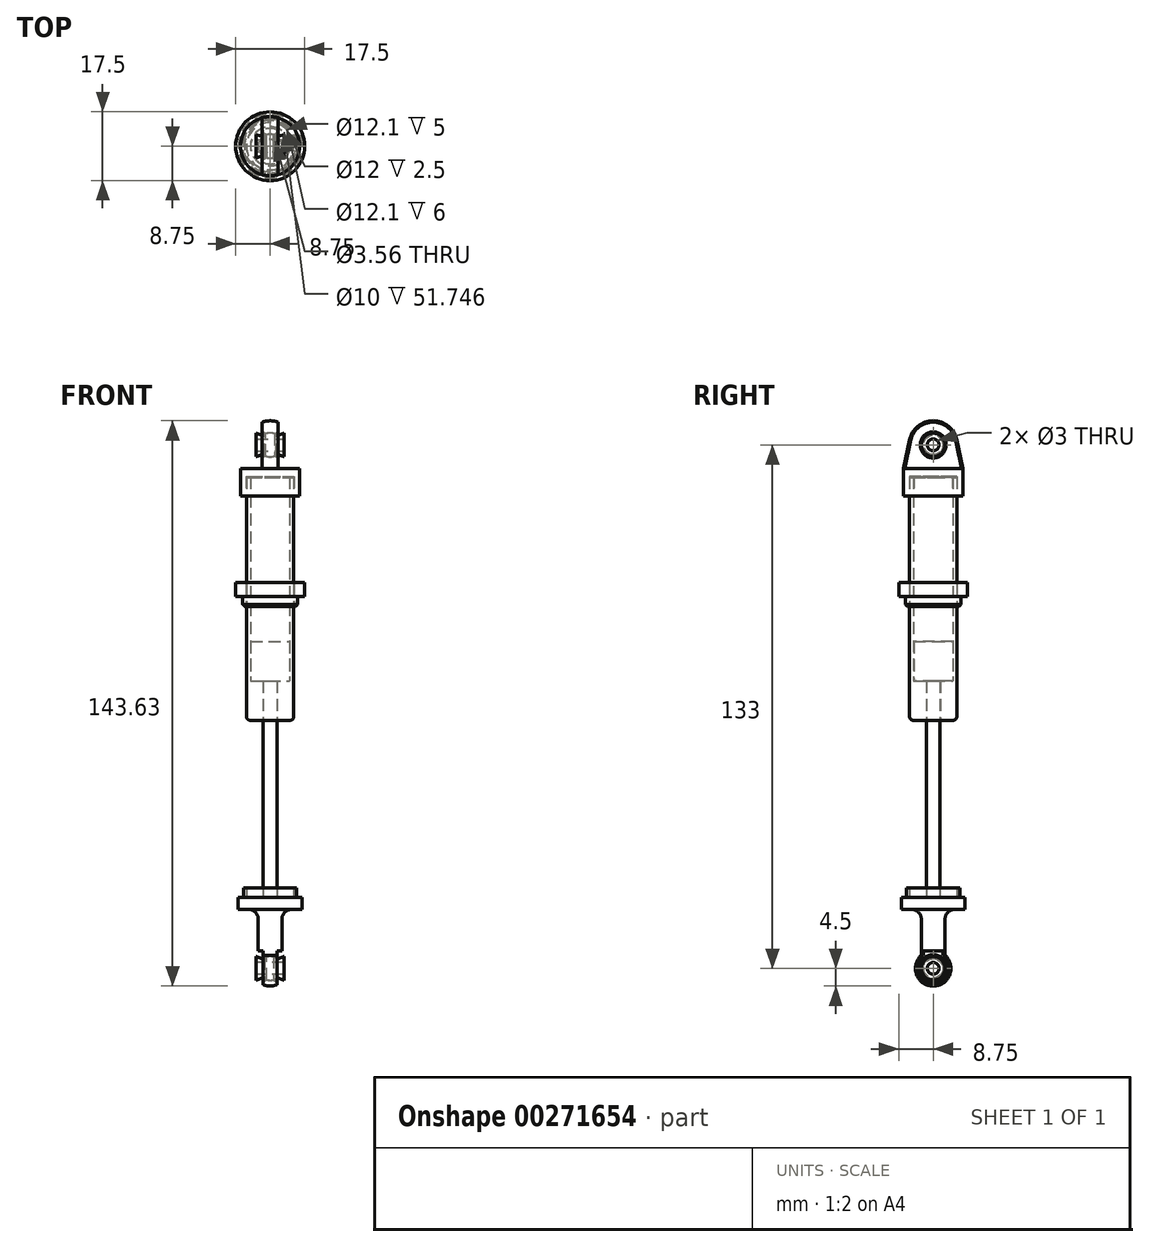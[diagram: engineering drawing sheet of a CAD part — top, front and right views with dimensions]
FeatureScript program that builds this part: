
annotation { "Feature Type Name" : "Feature", "Feature Type Description" : "" }
export const myFeature = defineFeature(function(context is Context, id is Id, definition is map)
    precondition{}
    {
        {
            var Q0;
            Q0=qCreatedBy(makeId("Front.planeOp"),FACE);
            var sketch = newSketch(context, id + "F0", { "sketchPlane" : qUnion([Q0])});
            skLineSegment(sketch, "E0", {"start": v(0, 0) * mm, "end": v(0, 317.47) * mm, "construction": true});
            skArc(sketch, "E1", {"start": v(0, 3) * mm, "mid": v(-3, 0) * mm, "end": v(0, -3) * mm});
            skLineSegment(sketch, "E2", {"start": v(0, 3) * mm, "end": v(0, -3) * mm});
            skArc(sketch, "E3", {"start": v(0, 3.05) * mm, "mid": v(-3.05, 0) * mm, "end": v(0, -3.05) * mm});
            skLineSegment(sketch, "E4", {"start": v(0, -3.05) * mm, "end": v(0, -4.5) * mm});
            skArc(sketch, "E5", {"start": v(-3, 3.35) * mm, "mid": v(-4.2, -1.6) * mm, "end": v(0, -4.5) * mm});
            skLineSegment(sketch, "E6", {"start": v(-3, 3.35) * mm, "end": v(-3, 12.46) * mm});
            skArc(sketch, "E7", {"start": v(-3, 12.46) * mm, "mid": v(-3.74, 14.26) * mm, "end": v(-5.54, 15) * mm});
            skLineSegment(sketch, "E8", {"start": v(-5.54, 15) * mm, "end": v(-8.1, 15) * mm});
            skLineSegment(sketch, "E9", {"start": v(-8.1, 15) * mm, "end": v(-8.1, 18) * mm});
            skLineSegment(sketch, "E10", {"start": v(-8.1, 18) * mm, "end": v(-6.75, 18) * mm});
            skLineSegment(sketch, "E11", {"start": v(-6.75, 18) * mm, "end": v(-6.75, 20.5) * mm});
            skLineSegment(sketch, "E12", {"start": v(-6.75, 20.5) * mm, "end": v(-6, 20.5) * mm});
            skLineSegment(sketch, "E13", {"start": v(-6, 20.5) * mm, "end": v(-6, 18) * mm});
            skLineSegment(sketch, "E14", {"start": v(-6, 18) * mm, "end": v(-1.75, 18) * mm});
            skLineSegment(sketch, "E15", {"start": v(-1.75, 18) * mm, "end": v(-1.75, 73.03) * mm});
            skLineSegment(sketch, "E16", {"start": v(-1.75, 73.03) * mm, "end": v(-4.95, 73.03) * mm});
            skLineSegment(sketch, "E17", {"start": v(-4.95, 73.03) * mm, "end": v(-4.95, 83.03) * mm});
            skLineSegment(sketch, "E18", {"start": v(-4.95, 83.03) * mm, "end": v(0, 83.03) * mm});
            skLineSegment(sketch, "E19", {"start": v(0, 83.03) * mm, "end": v(0, 3.05) * mm});
            skLineSegment(sketch, "E20", {"start": v(-1.78, 63) * mm, "end": v(-5, 63) * mm});
            skLineSegment(sketch, "E21", {"start": v(-6, 64) * mm, "end": v(-6, 124.75) * mm});
            skLineSegment(sketch, "E22", {"start": v(-1.78, 63) * mm, "end": v(-1.78, 73) * mm});
            skLineSegment(sketch, "E23", {"start": v(-1.78, 73) * mm, "end": v(-5, 73) * mm});
            skLineSegment(sketch, "E24", {"start": v(-5, 73) * mm, "end": v(-5, 124.75) * mm});
            skLineSegment(sketch, "E25", {"start": v(-7.5, 120) * mm, "end": v(-7.5, 127) * mm});
            skLineSegment(sketch, "E26", {"start": v(-7.5, 127) * mm, "end": v(-6, 134.24) * mm});
            skArc(sketch, "E27", {"start": v(0, 139.13) * mm, "mid": v(-3.87, 137.75) * mm, "end": v(-6, 134.24) * mm});
            skArc(sketch, "E28", {"start": v(0, 136) * mm, "mid": v(-3, 133) * mm, "end": v(0, 130) * mm});
            skArc(sketch, "E29", {"start": v(0, 136.05) * mm, "mid": v(-3.05, 133) * mm, "end": v(0, 129.95) * mm});
            skLineSegment(sketch, "E30", {"start": v(0, 136) * mm, "end": v(0, 130) * mm});
            skLineSegment(sketch, "E31", {"start": v(0, 136.05) * mm, "end": v(0, 139.13) * mm});
            skLineSegment(sketch, "E32", {"start": v(0, 129.95) * mm, "end": v(0, 119.92) * mm});
            skPoint(sketch, "E33.visualSharp", {"position": v(-6, 63) * mm});
            skArc(sketch, "E33.filletArc", {"start": v(-6, 64) * mm, "mid": v(-5.7, 63.3) * mm, "end": v(-5, 63) * mm});
            skLineSegment(sketch, "E34", {"start": v(-6.05, 92) * mm, "end": v(-6.05, 98) * mm});
            skLineSegment(sketch, "E35", {"start": v(-6.05, 98) * mm, "end": v(-8.75, 98) * mm});
            skLineSegment(sketch, "E36", {"start": v(-8.75, 98) * mm, "end": v(-8.75, 94.5) * mm});
            skLineSegment(sketch, "E37", {"start": v(-8.75, 94.5) * mm, "end": v(-7, 94.5) * mm});
            skLineSegment(sketch, "E38", {"start": v(-7, 94.5) * mm, "end": v(-7, 92.5) * mm});
            skLineSegment(sketch, "E39", {"start": v(-7, 92.5) * mm, "end": v(-6.5, 92) * mm});
            skLineSegment(sketch, "E40", {"start": v(-6.5, 92) * mm, "end": v(-6.05, 92) * mm});
            skLineSegment(sketch, "E41", {"start": v(-6, 124.75) * mm, "end": v(-5, 124.75) * mm});
            skLineSegment(sketch, "E42", {"start": v(-7.5, 120) * mm, "end": v(-6.05, 120) * mm});
            skLineSegment(sketch, "E43", {"start": v(-6.05, 120) * mm, "end": v(-6.05, 125) * mm});
            skLineSegment(sketch, "E44", {"start": v(-6.05, 125) * mm, "end": v(-4.95, 125) * mm});
            skLineSegment(sketch, "E45", {"start": v(-4.95, 125) * mm, "end": v(-4.95, 119.92) * mm});
            skLineSegment(sketch, "E46", {"start": v(-4.95, 119.92) * mm, "end": v(0, 119.92) * mm});
            skSolve(sketch);
        }
        {
            var Q0;
            Q0=qSketchRegion(id+"F0",true);
            var Q1;
            Q1=sQuery(id+"F0.wireOp",EDGE,"E0");
            revolve(context, id + "F1", {"entities" : qUnion([Q0]), "axis" : qUnion([Q1]), "revolveType" : RevolveType.FULL});
        }
        {
            var Q0;
            Q0=qCreatedBy(makeId("Front.planeOp"),FACE);
            var sketch = newSketch(context, id + "F2", { "sketchPlane" : qUnion([Q0])});
            skLineSegment(sketch, "E47", {"start": v(0, -24.47) * mm, "end": v(0, 246.9) * mm, "construction": true});
            skLineSegment(sketch, "E48.bottom", {"start": v(-1.75, 4.5) * mm, "end": v(-17.5, 4.5) * mm});
            skLineSegment(sketch, "E48.top", {"start": v(-1.75, -4.5) * mm, "end": v(-17.5, -4.5) * mm});
            skLineSegment(sketch, "E48.left", {"start": v(-1.75, 4.5) * mm, "end": v(-1.75, -4.5) * mm});
            skLineSegment(sketch, "E48.right", {"start": v(-17.5, 4.5) * mm, "end": v(-17.5, -4.5) * mm});
            skLineSegment(sketch, "E49.MirrorCS", {"start": v(1.75, 4.5) * mm, "end": v(17.5, 4.5) * mm});
            skLineSegment(sketch, "E50.MirrorCS", {"start": v(1.75, 4.5) * mm, "end": v(1.75, -4.5) * mm});
            skLineSegment(sketch, "E51.MirrorCS", {"start": v(1.75, -4.5) * mm, "end": v(17.5, -4.5) * mm});
            skLineSegment(sketch, "E52.MirrorCS", {"start": v(17.5, 4.5) * mm, "end": v(17.5, -4.5) * mm});
            skLineSegment(sketch, "E53.bottom", {"start": v(-2, 139.13) * mm, "end": v(-17.5, 139.13) * mm});
            skLineSegment(sketch, "E53.top", {"start": v(-2, 127) * mm, "end": v(-17.5, 127) * mm});
            skLineSegment(sketch, "E53.left", {"start": v(-2, 139.13) * mm, "end": v(-2, 127) * mm});
            skLineSegment(sketch, "E53.right", {"start": v(-17.5, 139.13) * mm, "end": v(-17.5, 127) * mm});
            skLineSegment(sketch, "E54.MirrorCS", {"start": v(17.5, 139.13) * mm, "end": v(17.5, 127) * mm});
            skLineSegment(sketch, "E55.MirrorCS", {"start": v(2, 127) * mm, "end": v(17.5, 127) * mm});
            skLineSegment(sketch, "E56.MirrorCS", {"start": v(2, 139.13) * mm, "end": v(17.5, 139.13) * mm});
            skLineSegment(sketch, "E57.MirrorCS", {"start": v(2, 139.13) * mm, "end": v(2, 127) * mm});
            skSolve(sketch);
        }
        {
            var Q0;
            Q0=qSketchRegion(id+"F2",true);
            extrude(context, id + "F3", {"entities" : qUnion([Q0]), "operationType" : NewBodyOperationType.REMOVE, "endBound" : BoundingType.THROUGH_ALL, "oppositeDirection" : true, "depth" : 25.4 * mm, "hasSecondDirection" : true, "secondDirectionBound" : BoundingType.THROUGH_ALL, "secondDirectionOppositeDirection" : false, "secondDirectionDepth" : 25.4 * mm});
        }
        {
            var Q0;
            Q0=makeQuery(id+"F3.boolean.opBoolean","INTERSECT",EDGE,{"derivedFrom":[makeQuery(id+"F1.opRevolve","SWEPT_FACE",FACE,{"disambiguationData":[OSD([sQuery(id+"F0.wireOp",EDGE,"E3")])]}),makeQuery(id+"F3.opExtrude","SWEPT_FACE",FACE,{"disambiguationData":[OSD([sQuery(id+"F2.wireOp",EDGE,"E48.left")])]})]});
            var Q1;
            Q1=makeQuery(id+"F3.boolean.opBoolean","INTERSECT",EDGE,{"derivedFrom":[makeQuery(id+"F1.opRevolve","SWEPT_FACE",FACE,{"disambiguationData":[OSD([sQuery(id+"F0.wireOp",EDGE,"E3")])]}),makeQuery(id+"F3.opExtrude","SWEPT_FACE",FACE,{"disambiguationData":[OSD([sQuery(id+"F2.wireOp",EDGE,"E50.MirrorCS")])]})]});
            chamfer(context, id + "F4", {"entities" : qUnion([Q0, Q1]), "width" : 1 * mm, "tangentPropagation" : true});
        }
        {
            var Q0;
            Q0=makeQuery(id+"F3.boolean.opBoolean","INTERSECT",EDGE,{"derivedFrom":[makeQuery(id+"F1.opRevolve","SWEPT_FACE",FACE,{"disambiguationData":[OSD([sQuery(id+"F0.wireOp",EDGE,"E29")])]}),makeQuery(id+"F3.opExtrude","SWEPT_FACE",FACE,{"disambiguationData":[OSD([sQuery(id+"F2.wireOp",EDGE,"E57.MirrorCS")])]})]});
            var Q1;
            Q1=makeQuery(id+"F3.boolean.opBoolean","INTERSECT",EDGE,{"derivedFrom":[makeQuery(id+"F1.opRevolve","SWEPT_FACE",FACE,{"disambiguationData":[OSD([sQuery(id+"F0.wireOp",EDGE,"E29")])]}),makeQuery(id+"F3.opExtrude","SWEPT_FACE",FACE,{"disambiguationData":[OSD([sQuery(id+"F2.wireOp",EDGE,"E53.left")])]})]});
            chamfer(context, id + "F5", {"entities" : qUnion([Q0, Q1]), "width" : 1 * mm, "tangentPropagation" : true});
        }
        {
            var Q0;
            Q0=qCreatedBy(makeId("Right.planeOp"),FACE);
            var sketch = newSketch(context, id + "F6", { "sketchPlane" : qUnion([Q0])});
            skCircle(sketch, "E58", {"center": v(0, 133) * mm, "radius": 2 * mm});
            skCircle(sketch, "E59", {"center": v(0, 0) * mm, "radius": 2 * mm});
            skSolve(sketch);
        }
        {
            var Q0;
            Q0=qSketchRegion(id+"F6",true);
            extrude(context, id + "F7", {"entities" : qUnion([Q0]), "operationType" : NewBodyOperationType.REMOVE, "endBound" : BoundingType.THROUGH_ALL, "oppositeDirection" : true, "depth" : 25.4 * mm, "hasSecondDirection" : true, "secondDirectionBound" : BoundingType.THROUGH_ALL, "secondDirectionOppositeDirection" : false, "secondDirectionDepth" : 25.4 * mm});
        }
        {
            var Q0;
            Q0=qCreatedBy(makeId("Front.planeOp"),FACE);
            var sketch = newSketch(context, id + "F8", { "sketchPlane" : qUnion([Q0])});
            skLineSegment(sketch, "E60", {"start": v(0, 133) * mm, "end": v(-42.18, 133) * mm, "construction": true});
            skLineSegment(sketch, "E61", {"start": v(0, 134.5) * mm, "end": v(-3.5, 134.5) * mm});
            skLineSegment(sketch, "E62", {"start": v(-3.5, 134.5) * mm, "end": v(-3.5, 136) * mm});
            skLineSegment(sketch, "E63", {"start": v(-3.5, 136) * mm, "end": v(-2.3, 135.55) * mm});
            skLineSegment(sketch, "E64", {"start": v(0, 133) * mm, "end": v(0, 223.2) * mm, "construction": true});
            skArc(sketch, "E65.0", {"start": v(0, 136) * mm, "mid": v(-0.76, 135.9) * mm, "end": v(-1.47, 135.62) * mm});
            skPoint(sketch, "E66.orphan", {"position": v(0, 130) * mm});
            skPoint(sketch, "E67.visualSharp", {"position": v(-1.83, 135.38) * mm});
            skArc(sketch, "E67.filletArc", {"start": v(-2.3, 135.55) * mm, "mid": v(-1.88, 135.5) * mm, "end": v(-1.47, 135.62) * mm});
            skArc(sketch, "E68.MirrorCS", {"start": v(0, 136) * mm, "mid": v(0.76, 135.9) * mm, "end": v(1.47, 135.62) * mm});
            skArc(sketch, "E69.MirrorCS", {"start": v(2.3, 135.55) * mm, "mid": v(1.88, 135.5) * mm, "end": v(1.47, 135.62) * mm});
            skLineSegment(sketch, "E70.MirrorCS", {"start": v(3.5, 136) * mm, "end": v(2.3, 135.55) * mm});
            skLineSegment(sketch, "E71.MirrorCS", {"start": v(3.5, 134.5) * mm, "end": v(3.5, 136) * mm});
            skLineSegment(sketch, "E72.MirrorCS", {"start": v(0, 134.5) * mm, "end": v(3.5, 134.5) * mm});
            skSolve(sketch);
        }
        {
            var Q0;
            Q0=qSketchRegion(id+"F8",true);
            var Q1;
            Q1=sQuery(id+"F8.wireOp",EDGE,"E60");
            revolve(context, id + "F9", {"operationType" : NewBodyOperationType.ADD, "entities" : qUnion([Q0]), "axis" : qUnion([Q1]), "revolveType" : RevolveType.FULL});
        }
        {
            var Q0;
            Q0=qCreatedBy(makeId("Front.planeOp"),FACE);
            var sketch = newSketch(context, id + "F10", { "sketchPlane" : qUnion([Q0])});
            skLineSegment(sketch, "E73", {"start": v(0, 0) * mm, "end": v(21.33, 0) * mm, "construction": true});
            skLineSegment(sketch, "E74", {"start": v(0, 1.5) * mm, "end": v(3.5, 1.5) * mm});
            skLineSegment(sketch, "E75", {"start": v(3.5, 1.5) * mm, "end": v(3.5, 3) * mm});
            skLineSegment(sketch, "E76", {"start": v(3.5, 3) * mm, "end": v(2.3, 2.55) * mm});
            skLineSegment(sketch, "E77", {"start": v(0, 0) * mm, "end": v(0, 6.77) * mm, "construction": true});
            skArc(sketch, "E78", {"start": v(1.47, 2.62) * mm, "mid": v(0.76, 2.9) * mm, "end": v(0, 3) * mm});
            skPoint(sketch, "E79.orphan", {"position": v(0, -3) * mm});
            skPoint(sketch, "E80.visualSharp", {"position": v(1.83, 2.38) * mm});
            skArc(sketch, "E80.filletArc", {"start": v(1.47, 2.62) * mm, "mid": v(1.88, 2.5) * mm, "end": v(2.3, 2.55) * mm});
            skArc(sketch, "E81.MirrorCS", {"start": v(-1.47, 2.62) * mm, "mid": v(-0.76, 2.9) * mm, "end": v(0, 3) * mm});
            skArc(sketch, "E82.MirrorCS", {"start": v(-1.47, 2.62) * mm, "mid": v(-1.88, 2.5) * mm, "end": v(-2.3, 2.55) * mm});
            skLineSegment(sketch, "E83.MirrorCS", {"start": v(-3.5, 3) * mm, "end": v(-2.3, 2.55) * mm});
            skLineSegment(sketch, "E84.MirrorCS", {"start": v(-3.5, 1.5) * mm, "end": v(-3.5, 3) * mm});
            skLineSegment(sketch, "E85.MirrorCS", {"start": v(0, 1.5) * mm, "end": v(-3.5, 1.5) * mm});
            skSolve(sketch);
        }
        {
            var Q0;
            Q0=qSketchRegion(id+"F10",true);
            var Q1;
            Q1=sQuery(id+"F10.wireOp",EDGE,"E73");
            revolve(context, id + "F11", {"operationType" : NewBodyOperationType.ADD, "entities" : qUnion([Q0]), "axis" : qUnion([Q1]), "revolveType" : RevolveType.FULL});
        }
    });
